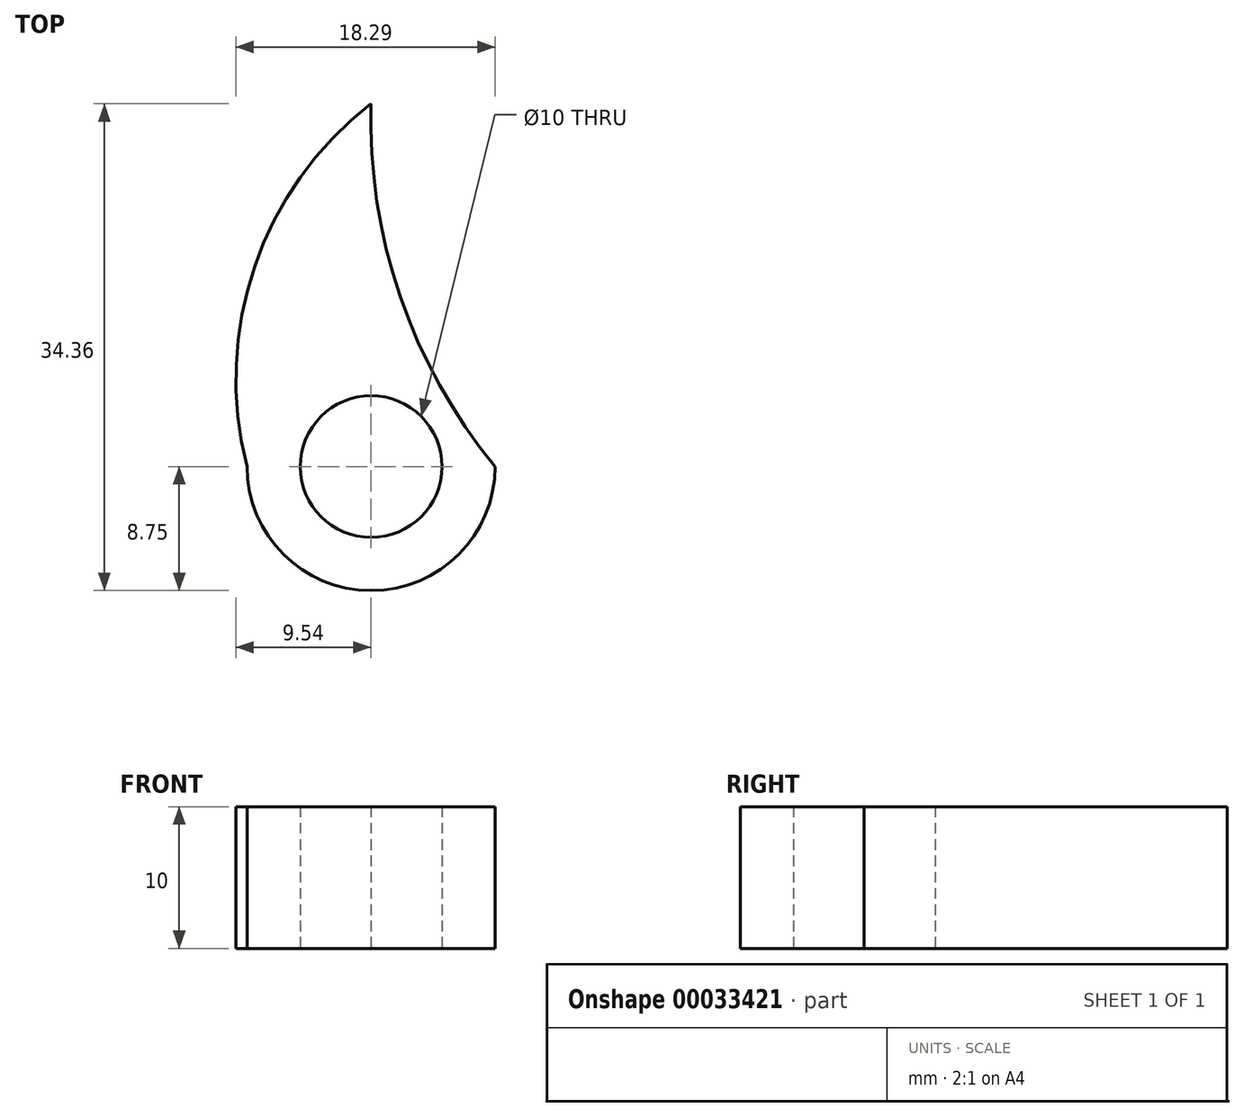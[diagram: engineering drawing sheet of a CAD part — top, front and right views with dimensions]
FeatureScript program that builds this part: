
annotation { "Feature Type Name" : "Feature", "Feature Type Description" : "" }
export const myFeature = defineFeature(function(context is Context, id is Id, definition is map)
    precondition{}
    {
        {
            var Q0;
            Q0=qCreatedBy(makeId("Top.planeOp"),FACE);
            var sketch = newSketch(context, id + "F0", { "sketchPlane" : qUnion([Q0])});
            skCircle(sketch, "E0", {"center": v(0, 0) * mm, "radius": 8.75 * mm});
            skArc(sketch, "E1", {"start": v(0, 25.61) * mm, "mid": v(-8.22, 14.12) * mm, "end": v(-8.75, 0) * mm});
            skArc(sketch, "E2", {"start": v(0, 25.61) * mm, "mid": v(2.05, 12.01) * mm, "end": v(8.75, 0) * mm});
            skCircle(sketch, "E3", {"center": v(0, 0) * mm, "radius": 5 * mm});
            skSolve(sketch);
        }
        {
            var Q0;
            {var subQ3=sQuery(id+"F0.wireOp",EDGE,"E1");Q0=makeQuery(id+"F0.imprint","IMPRINT",FACE,{"disambiguationData":[TD([[makeQuery(id+"F0.imprint","IMPRINT",EDGE,{"derivedFrom":subQ3}),1.0]])]});}
            var Q1;
            Q1=makeQuery(id+"F0.imprint","IMPRINT",FACE,{"disambiguationData":[TD([[makeQuery(id+"F0.imprint","IMPRINT",EDGE,{"derivedFrom":sQuery(id+"F0.wireOp",EDGE,"E3")}),-1.0]])]});
            var Q2;
            {var subQ0=sQuery(id+"F0.wireOp",EDGE,"E2");var subQ1=sQuery(id+"F0.wireOp",EDGE,"E0");var subQ3=makeQuery(id+"F0.imprint","INTERSECT",VERTEX,{"disambiguationData":[OD(0.0)],"derivedFrom":[subQ1,subQ0]});Q2=makeQuery(id+"F0.imprint","IMPRINT",FACE,{"disambiguationData":[TD([[makeQuery(id+"F0.imprint","IMPRINT",EDGE,{"disambiguationData":[TD([[subQ3,-1.0]])],"derivedFrom":subQ1}),1.0]])]});}
            extrude(context, id + "F1", {"entities" : qUnion([Q0, Q1, Q2]), "depth" : 10 * mm});
        }
    });
